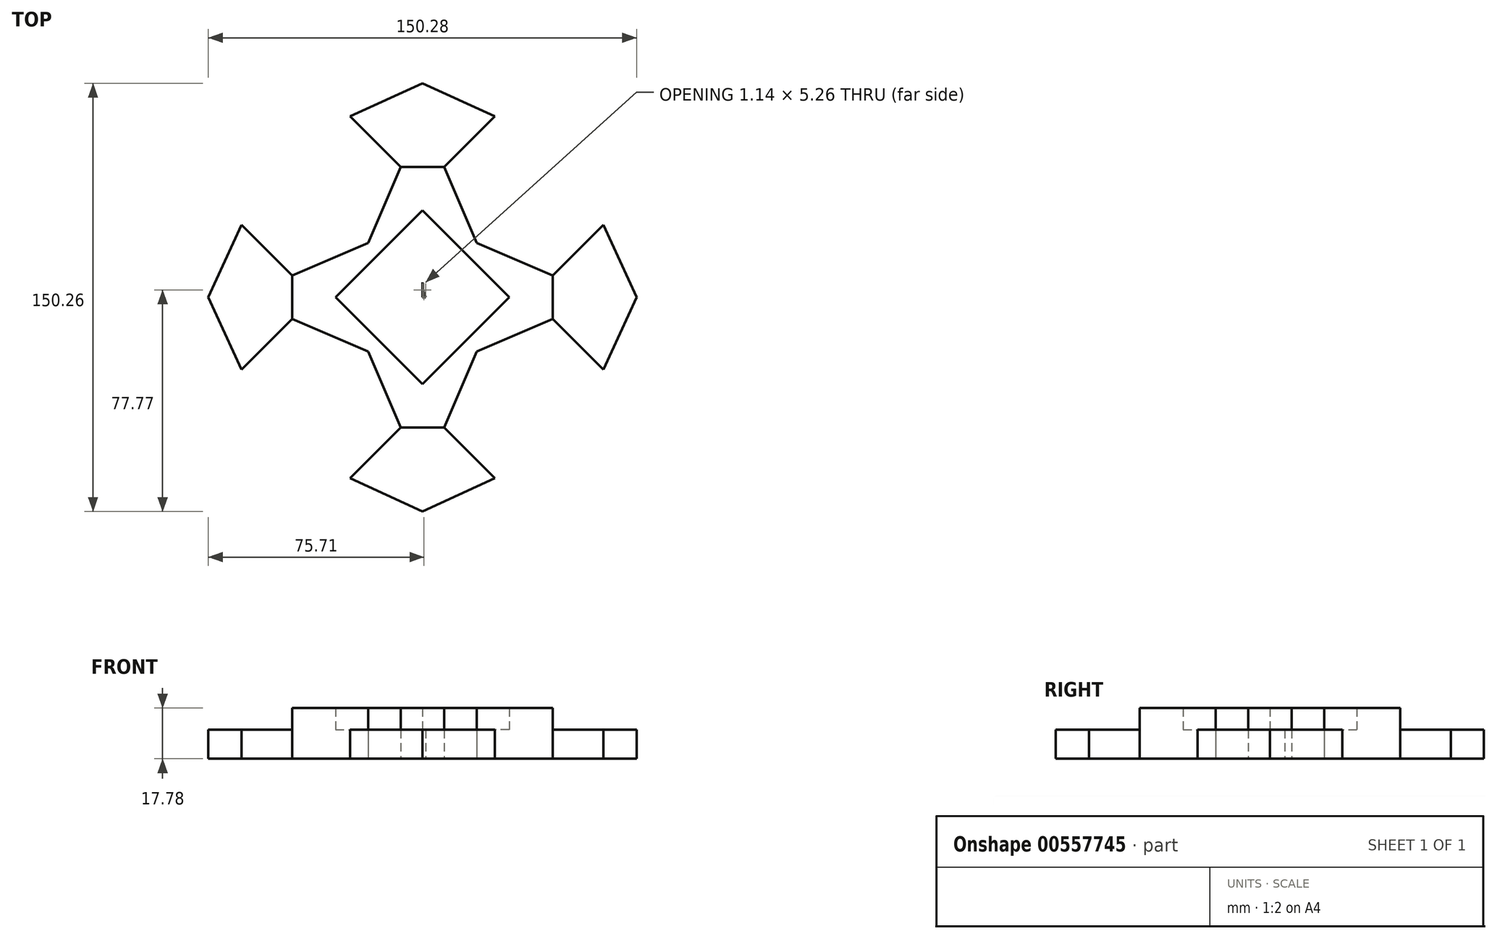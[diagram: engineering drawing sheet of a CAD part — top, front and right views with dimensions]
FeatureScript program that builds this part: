
annotation { "Feature Type Name" : "Feature", "Feature Type Description" : "" }
export const myFeature = defineFeature(function(context is Context, id is Id, definition is map)
    precondition{}
    {
        {
            var Q0;
            Q0=qCreatedBy(makeId("Top.planeOp"),FACE);
            var sketch = newSketch(context, id + "F0", { "sketchPlane" : qUnion([Q0])});
            skLineSegment(sketch, "E0", {"start": v(0, 0) * mm, "end": v(0, 63.5) * mm});
            skLineSegment(sketch, "E1", {"start": v(0, 0) * mm, "end": v(63.5, 0) * mm});
            skLineSegment(sketch, "E2", {"start": v(0, 0) * mm, "end": v(0, -63.5) * mm});
            skLineSegment(sketch, "E3", {"start": v(0, 0) * mm, "end": v(-63.5, 0) * mm});
            skLineSegment(sketch, "E4", {"start": v(0, 5.26) * mm, "end": v(0, 38.1) * mm});
            skLineSegment(sketch, "E5", {"start": v(0, 0) * mm, "end": v(38.1, 0) * mm});
            skLineSegment(sketch, "E6", {"start": v(0, 0) * mm, "end": v(0, -38.1) * mm});
            skLineSegment(sketch, "E7", {"start": v(0, 0) * mm, "end": v(-38.1, 0) * mm});
            skLineSegment(sketch, "E8", {"start": v(-38.1, 0) * mm, "end": v(0, -38.1) * mm});
            skLineSegment(sketch, "E9", {"start": v(0, -38.1) * mm, "end": v(38.1, 0) * mm});
            skLineSegment(sketch, "E10", {"start": v(38.1, 0) * mm, "end": v(0, 38.1) * mm});
            skLineSegment(sketch, "E11", {"start": v(0, 38.1) * mm, "end": v(-38.1, 0) * mm});
            skLineSegment(sketch, "E12", {"start": v(0, 0) * mm, "end": v(-19.05, 19.05) * mm});
            skLineSegment(sketch, "E13", {"start": v(0, 0) * mm, "end": v(19.05, 19.05) * mm});
            skLineSegment(sketch, "E14", {"start": v(3.72, -3.72) * mm, "end": v(19.05, -19.05) * mm});
            skLineSegment(sketch, "E15", {"start": v(0, 0) * mm, "end": v(-19.05, -19.05) * mm});
            skLineSegment(sketch, "E16", {"start": v(0, 63.5) * mm, "end": v(19.05, 19.05) * mm});
            skLineSegment(sketch, "E17", {"start": v(63.5, 0) * mm, "end": v(19.05, 19.05) * mm});
            skLineSegment(sketch, "E18", {"start": v(19.05, -19.05) * mm, "end": v(63.5, 0) * mm});
            skLineSegment(sketch, "E19", {"start": v(19.05, -19.05) * mm, "end": v(0, -63.5) * mm});
            skLineSegment(sketch, "E20", {"start": v(-19.05, -19.05) * mm, "end": v(0, -63.5) * mm});
            skLineSegment(sketch, "E21", {"start": v(-19.05, -19.05) * mm, "end": v(-63.5, 0) * mm});
            skLineSegment(sketch, "E22", {"start": v(-19.05, 19.05) * mm, "end": v(0, 63.5) * mm});
            skLineSegment(sketch, "E23", {"start": v(-19.05, 19.05) * mm, "end": v(-63.5, 0) * mm});
            skLineSegment(sketch, "E24", {"start": v(-38.1, 0) * mm, "end": v(-63.5, 25.4) * mm});
            skLineSegment(sketch, "E25", {"start": v(-38.1, 0) * mm, "end": v(-63.5, -25.4) * mm});
            skLineSegment(sketch, "E26", {"start": v(-63.5, -25.4) * mm, "end": v(-75.14, 0) * mm});
            skLineSegment(sketch, "E27", {"start": v(-75.14, 0) * mm, "end": v(-63.5, 25.4) * mm});
            skLineSegment(sketch, "E28", {"start": v(0, -38.1) * mm, "end": v(25.4, -63.5) * mm});
            skLineSegment(sketch, "E29", {"start": v(0, -38.1) * mm, "end": v(-25.4, -63.5) * mm});
            skLineSegment(sketch, "E30", {"start": v(25.4, -63.5) * mm, "end": v(0, -75.14) * mm});
            skLineSegment(sketch, "E31", {"start": v(-25.4, -63.5) * mm, "end": v(0, -75.14) * mm});
            skLineSegment(sketch, "E32", {"start": v(38.1, 0) * mm, "end": v(63.5, 25.4) * mm});
            skLineSegment(sketch, "E33", {"start": v(38.1, 0) * mm, "end": v(63.5, -25.4) * mm});
            skLineSegment(sketch, "E34", {"start": v(63.5, 25.4) * mm, "end": v(75.14, 0) * mm});
            skLineSegment(sketch, "E35", {"start": v(75.14, 0) * mm, "end": v(63.5, -25.4) * mm});
            skLineSegment(sketch, "E36", {"start": v(0, 38.1) * mm, "end": v(25.4, 63.5) * mm});
            skLineSegment(sketch, "E37", {"start": v(0, 38.1) * mm, "end": v(-25.4, 63.5) * mm});
            skLineSegment(sketch, "E38", {"start": v(-25.4, 63.5) * mm, "end": v(0, 75.12) * mm});
            skLineSegment(sketch, "E39", {"start": v(25.4, 63.5) * mm, "end": v(0, 75.12) * mm});
            skPoint(sketch, "E40.visualSharp", {"position": v(0, 0) * mm});
            skArc(sketch, "E40.filletArc", {"start": v(0, 5.26) * mm, "mid": v(0.97, 0.4) * mm, "end": v(3.72, -3.72) * mm});
            skSolve(sketch);
        }
        {
            var Q0;
            Q0 = qSketchRegion(id + "F0", true);
            var Q1;
            Q1 = qSketchRegion(id + "F5", true);
            extrude(context, id + "F1", {"entities" : qUnion([Q0, Q1]), "depth" : 10.16 * mm, "offsetDistance" : 25.4 * mm});
        }
        {
            var Q0;
            Q0=makeQuery(id+"F1.opExtrude","CAP_FACE",FACE,{"disambiguationData":[OSD([sQuery(id+"F0.wireOp",EDGE,"E0"),sQuery(id+"F0.wireOp",EDGE,"E5"),sQuery(id+"F0.wireOp",EDGE,"E16"),sQuery(id+"F0.wireOp",EDGE,"E17"),sQuery(id+"F0.wireOp",EDGE,"E18"),sQuery(id+"F0.wireOp",EDGE,"E19"),sQuery(id+"F0.wireOp",EDGE,"E20"),sQuery(id+"F0.wireOp",EDGE,"E21"),sQuery(id+"F0.wireOp",EDGE,"E22"),sQuery(id+"F0.wireOp",EDGE,"E23"),sQuery(id+"F0.wireOp",EDGE,"E24"),sQuery(id+"F0.wireOp",EDGE,"E25"),sQuery(id+"F0.wireOp",EDGE,"E26"),sQuery(id+"F0.wireOp",EDGE,"E27"),sQuery(id+"F0.wireOp",EDGE,"E28"),sQuery(id+"F0.wireOp",EDGE,"E29"),sQuery(id+"F0.wireOp",EDGE,"E30"),sQuery(id+"F0.wireOp",EDGE,"E31"),sQuery(id+"F0.wireOp",EDGE,"E32"),sQuery(id+"F0.wireOp",EDGE,"E33"),sQuery(id+"F0.wireOp",EDGE,"E34"),sQuery(id+"F0.wireOp",EDGE,"E35"),sQuery(id+"F0.wireOp",EDGE,"E36"),sQuery(id+"F0.wireOp",EDGE,"E37"),sQuery(id+"F0.wireOp",EDGE,"E38"),sQuery(id+"F0.wireOp",EDGE,"E39"),sQuery(id+"F0.wireOp",EDGE,"E40.filletArc")])],"isStart":false});
            var sketch = newSketch(context, id + "F2", { "sketchPlane" : qUnion([Q0])});
            skLineSegment(sketch, "E41", {"start": v(0, 0) * mm, "end": v(-30.48, 0) * mm});
            skLineSegment(sketch, "E42", {"start": v(0, 0) * mm, "end": v(0, -30.48) * mm});
            skLineSegment(sketch, "E43", {"start": v(0, 0) * mm, "end": v(30.48, 0) * mm});
            skLineSegment(sketch, "E44", {"start": v(0, 0) * mm, "end": v(0, 30.48) * mm});
            skLineSegment(sketch, "E45", {"start": v(-45.72, 7.62) * mm, "end": v(-45.72, -7.62) * mm});
            skLineSegment(sketch, "E46", {"start": v(-7.62, -45.72) * mm, "end": v(7.62, -45.72) * mm});
            skLineSegment(sketch, "E47", {"start": v(45.72, -7.62) * mm, "end": v(45.72, 7.62) * mm});
            skLineSegment(sketch, "E48", {"start": v(7.62, 45.72) * mm, "end": v(-7.62, 45.72) * mm});
            skLineSegment(sketch, "E49", {"start": v(0, 30.48) * mm, "end": v(30.48, 0) * mm});
            skLineSegment(sketch, "E50", {"start": v(30.48, 0) * mm, "end": v(0, -30.48) * mm});
            skLineSegment(sketch, "E51", {"start": v(0, -30.48) * mm, "end": v(-30.48, 0) * mm});
            skLineSegment(sketch, "E52", {"start": v(-30.48, 0) * mm, "end": v(0, 30.48) * mm});
            skSolve(sketch);
        }
        {
            var Q0;
            Q0=makeQuery(id+"F2.imprint","IMPRINT",FACE,{"disambiguationData":[TD([[makeQuery(id+"F2.imprint","IMPRINT",EDGE,{"derivedFrom":sQuery(id+"F2.wireOp",EDGE,"E45")}),1.0]])]});
            extrude(context, id + "F3", {"entities" : qUnion([Q0]), "operationType" : NewBodyOperationType.ADD, "depth" : 7.62 * mm, "offsetDistance" : 25.4 * mm});
        }
    });
